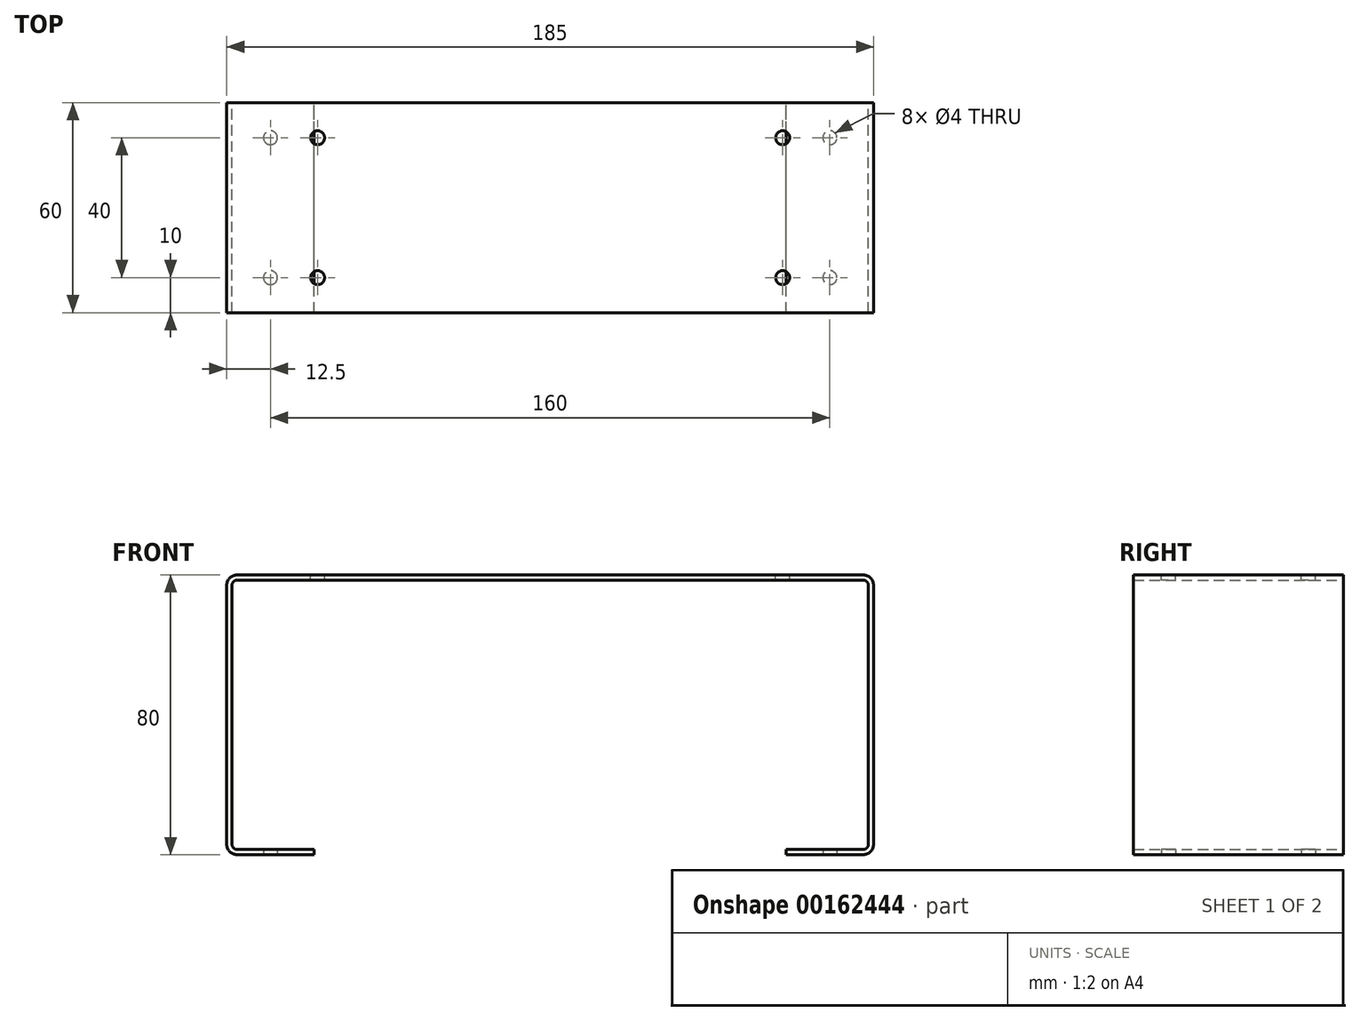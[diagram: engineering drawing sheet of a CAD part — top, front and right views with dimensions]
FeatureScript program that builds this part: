
annotation { "Feature Type Name" : "Feature", "Feature Type Description" : "" }
export const myFeature = defineFeature(function(context is Context, id is Id, definition is map)
    precondition{}
    {
        {
            var Q0;
            Q0=qCreatedBy(makeId("Front.planeOp"),FACE);
            var sketch = newSketch(context, id + "F0", { "sketchPlane" : qUnion([Q0])});
            skLineSegment(sketch, "E0", {"start": v(0, 80) * mm, "end": v(-92.5, 80) * mm});
            skLineSegment(sketch, "E1", {"start": v(-92.5, 80) * mm, "end": v(-92.5, 0) * mm});
            skLineSegment(sketch, "E2.0", {"start": v(-91, 1.5) * mm, "end": v(-67.5, 1.5) * mm});
            skLineSegment(sketch, "E2.1", {"start": v(-91, 78.5) * mm, "end": v(-91, 1.5) * mm});
            skLineSegment(sketch, "E2.2", {"start": v(0, 78.5) * mm, "end": v(-91, 78.5) * mm});
            skLineSegment(sketch, "E3", {"start": v(-67.5, 1.5) * mm, "end": v(-67.5, 0) * mm});
            skLineSegment(sketch, "E4", {"start": v(-92.5, 0) * mm, "end": v(-67.5, 0) * mm});
            skLineSegment(sketch, "E5.MirrorCS", {"start": v(67.5, 1.5) * mm, "end": v(67.5, 0) * mm});
            skLineSegment(sketch, "E6.MirrorCS", {"start": v(0, 80) * mm, "end": v(92.5, 80) * mm});
            skLineSegment(sketch, "E7.MirrorCS", {"start": v(91, 78.5) * mm, "end": v(91, 1.5) * mm});
            skLineSegment(sketch, "E8.MirrorCS", {"start": v(0, 78.5) * mm, "end": v(91, 78.5) * mm});
            skLineSegment(sketch, "E9.MirrorCS", {"start": v(92.5, 80) * mm, "end": v(92.5, 0) * mm});
            skLineSegment(sketch, "E10.MirrorCS", {"start": v(92.5, 0) * mm, "end": v(67.5, 0) * mm});
            skLineSegment(sketch, "E11.MirrorCS", {"start": v(91, 1.5) * mm, "end": v(67.5, 1.5) * mm});
            skSolve(sketch);
        }
        {
            var Q0;
            Q0 = qSketchRegion(id + "F0", true);
            extrude(context, id + "F1", {"entities" : qUnion([Q0]), "endBound" : BoundingType.SYMMETRIC, "depth" : 60 * mm});
        }
        {
            var Q0;
            Q0=makeQuery(id+"F1.opExtrude","SWEPT_FACE",FACE,{"disambiguationData":[OSD([sQuery(id+"F0.wireOp",EDGE,"E0"),sQuery(id+"F0.wireOp",EDGE,"E6.MirrorCS")])]});
            var sketch = newSketch(context, id + "F2", { "sketchPlane" : qUnion([Q0])});
            skLineSegment(sketch, "E12", {"start": v(0, 0) * mm, "end": v(66.5, 0) * mm, "construction": true});
            skLineSegment(sketch, "E13", {"start": v(66.5, 0) * mm, "end": v(66.5, 20) * mm, "construction": true});
            skLineSegment(sketch, "E14", {"start": v(66.5, 0) * mm, "end": v(66.5, -20) * mm, "construction": true});
            skLineSegment(sketch, "E15.MirrorCS", {"start": v(0, 0) * mm, "end": v(-66.5, 0) * mm, "construction": true});
            skLineSegment(sketch, "E16.MirrorCS", {"start": v(-66.5, 0) * mm, "end": v(-66.5, -20) * mm, "construction": true});
            skLineSegment(sketch, "E17.MirrorCS", {"start": v(-66.5, 0) * mm, "end": v(-66.5, 20) * mm, "construction": true});
            skCircle(sketch, "E18", {"center": v(-66.5, 20) * mm, "radius": 2 * mm});
            skCircle(sketch, "E19", {"center": v(-66.5, -20) * mm, "radius": 2 * mm});
            skCircle(sketch, "E20", {"center": v(66.5, 20) * mm, "radius": 2 * mm});
            skCircle(sketch, "E21", {"center": v(66.5, -20) * mm, "radius": 2 * mm});
            skSolve(sketch);
        }
        {
            var Q0;
            Q0 = qSketchRegion(id + "F2", true);
            extrude(context, id + "F3", {"entities" : qUnion([Q0]), "operationType" : NewBodyOperationType.REMOVE, "oppositeDirection" : true, "depth" : 25 * mm});
        }
        {
            var Q0;
            Q0=makeQuery(id+"F1.opExtrude","SWEPT_FACE",FACE,{"disambiguationData":[OSD([sQuery(id+"F0.wireOp",EDGE,"E4")])]});
            var sketch = newSketch(context, id + "F4", { "sketchPlane" : qUnion([Q0])});
            skLineSegment(sketch, "E22", {"start": v(-80, 30) * mm, "end": v(-80, -30) * mm, "construction": true});
            skLineSegment(sketch, "E23", {"start": v(-67.5, 0) * mm, "end": v(-92.5, 0) * mm, "construction": true});
            skCircle(sketch, "E24", {"center": v(-80, 20) * mm, "radius": 2 * mm});
            skCircle(sketch, "E25", {"center": v(-80, -20) * mm, "radius": 2 * mm});
            skCircle(sketch, "E26.MirrorC", {"center": v(80, -20) * mm, "radius": 2 * mm});
            skCircle(sketch, "E27.MirrorC", {"center": v(80, 20) * mm, "radius": 2 * mm});
            skSolve(sketch);
        }
        {
            var Q0;
            Q0 = qSketchRegion(id + "F4", true);
            extrude(context, id + "F5", {"entities" : qUnion([Q0]), "operationType" : NewBodyOperationType.REMOVE, "oppositeDirection" : true, "depth" : 10 * mm});
        }
        {
            var Q0;
            Q0=makeQuery(id+"F1.opExtrude","SWEPT_EDGE",EDGE,{"disambiguationData":[OSD([sQuery(id+"F0.wireOp",EDGE,"E0"),sQuery(id+"F0.wireOp",EDGE,"E1")])]});
            var Q1;
            Q1=makeQuery(id+"F1.opExtrude","SWEPT_EDGE",EDGE,{"disambiguationData":[OSD([sQuery(id+"F0.wireOp",EDGE,"E1"),sQuery(id+"F0.wireOp",EDGE,"E4")])]});
            var Q2;
            Q2=makeQuery(id+"F1.opExtrude","SWEPT_EDGE",EDGE,{"disambiguationData":[OSD([sQuery(id+"F0.wireOp",EDGE,"E6.MirrorCS"),sQuery(id+"F0.wireOp",EDGE,"E9.MirrorCS")])]});
            var Q3;
            Q3=makeQuery(id+"F1.opExtrude","SWEPT_EDGE",EDGE,{"disambiguationData":[OSD([sQuery(id+"F0.wireOp",EDGE,"E9.MirrorCS"),sQuery(id+"F0.wireOp",EDGE,"E10.MirrorCS")])]});
            fillet(context, id + "F6", {"entities" : qUnion([Q0, Q1, Q2, Q3]), "radius" : 3 * mm, "tangentPropagation" : true, "allowEdgeOverflow" : false});
        }
        {
            var Q0;
            Q0=makeQuery(id+"F1.opExtrude","SWEPT_EDGE",EDGE,{"disambiguationData":[OSD([sQuery(id+"F0.wireOp",EDGE,"E2.1"),sQuery(id+"F0.wireOp",EDGE,"E2.2")])]});
            var Q1;
            Q1=makeQuery(id+"F1.opExtrude","SWEPT_EDGE",EDGE,{"disambiguationData":[OSD([sQuery(id+"F0.wireOp",EDGE,"E7.MirrorCS"),sQuery(id+"F0.wireOp",EDGE,"E8.MirrorCS")])]});
            var Q2;
            Q2=makeQuery(id+"F1.opExtrude","SWEPT_EDGE",EDGE,{"disambiguationData":[OSD([sQuery(id+"F0.wireOp",EDGE,"E2.0"),sQuery(id+"F0.wireOp",EDGE,"E2.1")])]});
            var Q3;
            Q3=makeQuery(id+"F1.opExtrude","SWEPT_EDGE",EDGE,{"disambiguationData":[OSD([sQuery(id+"F0.wireOp",EDGE,"E7.MirrorCS"),sQuery(id+"F0.wireOp",EDGE,"E11.MirrorCS")])]});
            fillet(context, id + "F7", {"entities" : qUnion([Q0, Q1, Q2, Q3]), "radius" : 1.5 * mm, "tangentPropagation" : true, "allowEdgeOverflow" : false});
        }
    });
